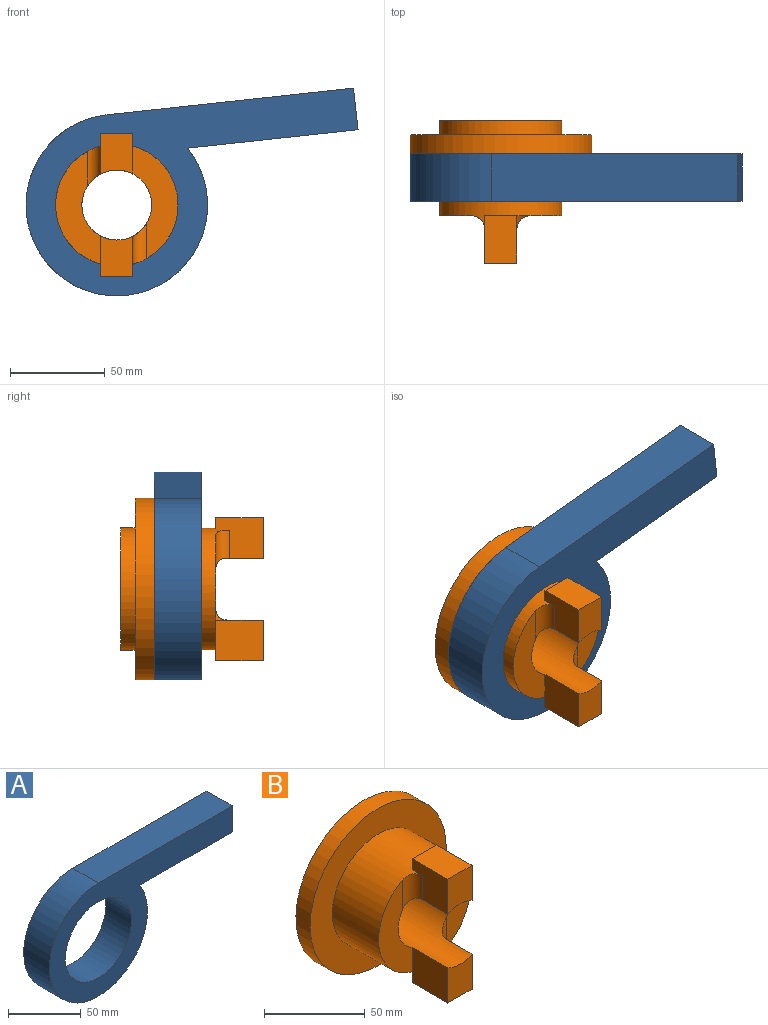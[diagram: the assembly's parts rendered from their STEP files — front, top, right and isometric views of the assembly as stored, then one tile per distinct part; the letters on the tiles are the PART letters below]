
ASSEMBLY  parts=2 mates=1
PART A: 7 faces, bbox 178.3x25x95.6 mm
  f0: cylinder r=47.82mm len=95.64mm, axis (0,1,0), area 6314.1mm2, adj f2,f3,f4,f5
  f1: cylinder r=32.22mm len=64.44mm, axis (0,1,0), area 5061.2mm2, adj f2,f3
  f2: plane 178.33x95.64mm, normal (0,-1,0), area 6174.4mm2, adj f0,f1,f4,f5,f6
  f3: plane 178.33x95.64mm, normal (0,1,0), area 6174.4mm2, adj f0,f1,f4,f5,f6
  f4: plane 130.51x25mm, normal (0,0,1), area 3262.7mm2, adj f0,f2,f3,f6
  f5: plane 90.23x25mm, normal (0,0,-1), area 2255.6mm2, adj f0,f2,f3,f6
  f6: plane 25x22.05mm, normal (1,0,0), area 551.3mm2, adj f2,f3,f4,f5
PART B: 21 faces, bbox 95.6x75x95.6 mm
  f0: plane 59.33x23.72mm, normal (0,-1,0), area 745.5mm2, adj f2,f3,f10,f20
  f1: cylinder r=32.22mm len=64.44mm, axis (0,1,0), area 1518.4mm2, adj f4,f7
  f2: cylinder r=18.41mm len=75mm, axis (0,1,0), area 6693.1mm2, adj f0,f4,f8,f10,f12,f13,f14,f15
  f3: cylinder r=32.22mm len=64.44mm, axis (0,1,0), area 6601.7mm2, adj f0,f6,f8,f9,f12,f14,f18,f19
  f4: plane 64.44x64.44mm, normal (0,1,0), area 2196.5mm2, adj f1,f2
  f5: cylinder r=47.82mm len=95.64mm, axis (0,1,0), area 3004.6mm2, adj f6,f7
  f6: plane 95.64x95.64mm, normal (0,-1,0), area 3922.7mm2, adj f3,f5
  f7: plane 95.64x95.64mm, normal (0,1,0), area 3922.7mm2, adj f1,f5
  f8: plane 59.33x23.72mm, normal (0,-1,0), area 745.5mm2, adj f2,f3,f15,f19
  f9: plane 17x6.57mm, normal (0,1,0), area 98.6mm2, adj f3,f10,f11,f12
  f10: plane 25x21.31mm, normal (1,0,0), area 532.8mm2, adj f0,f2,f9,f11,f13
  f11: plane 25x17mm, normal (0,0,1), area 425mm2, adj f9,f10,f12,f13
  f12: plane 25x21.31mm, normal (-1,0,0), area 429.6mm2, adj f2,f3,f9,f11,f13,f19
  f13: plane 21.31x17mm, normal (0,-1,0), area 338.5mm2, adj f2,f10,f11,f12
  f14: plane 25x21.31mm, normal (1,0,0), area 429.6mm2, adj f2,f3,f16,f17,f18,f20
  f15: plane 25x21.31mm, normal (-1,0,0), area 532.8mm2, adj f2,f8,f16,f17,f18
  f16: plane 25x17mm, normal (0,0,-1), area 425mm2, adj f14,f15,f17,f18
  f17: plane 21.31x17mm, normal (0,-1,0), area 338.5mm2, adj f2,f14,f15,f16
  f18: plane 17x6.57mm, normal (0,1,0), area 98.6mm2, adj f3,f14,f15,f16
  f19: cylinder r=7mm len=21.14mm, axis (0,0,-1), area 172.9mm2, adj f2,f3,f8,f12
  f20: cylinder r=7mm len=21.14mm, axis (0,0,1), area 172.9mm2, adj f0,f2,f3,f14
PLACE A rot(axis=(0,-1,0),6.2deg) t=(0,0,0)mm
PLACE B at identity fixed
MATE revolute A.f1 <-> B.f1  axis (0,1,0) through (0,-5,0)mm
